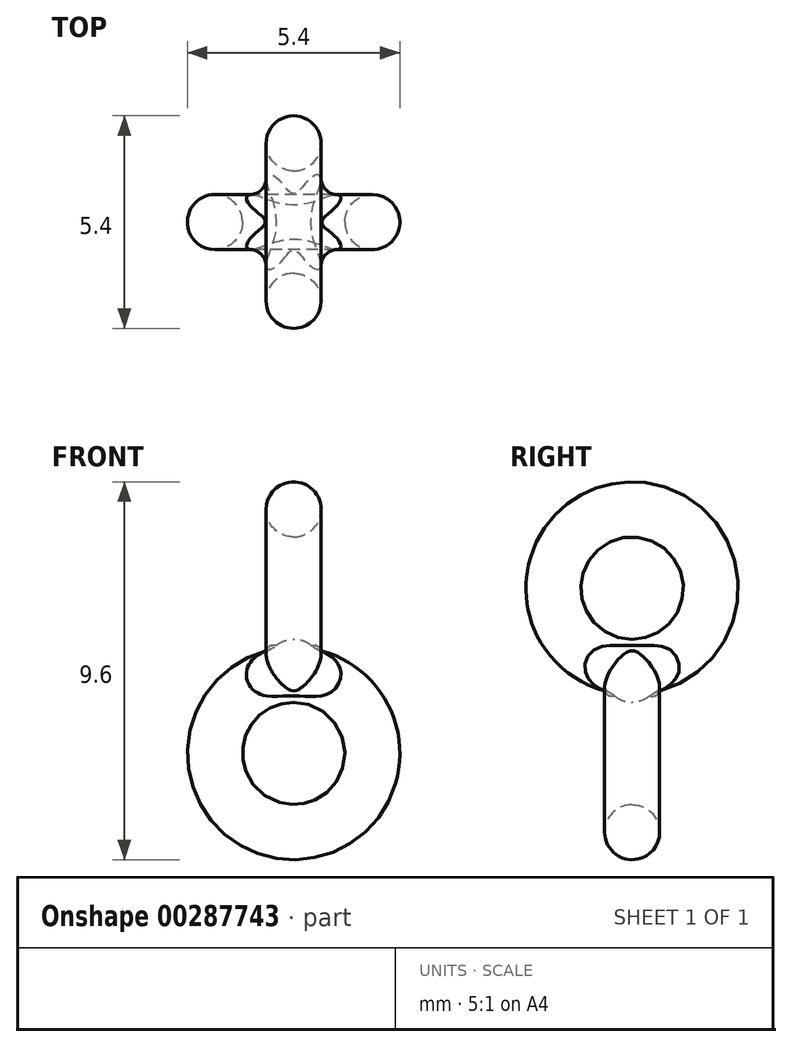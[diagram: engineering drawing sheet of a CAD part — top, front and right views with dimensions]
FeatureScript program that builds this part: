
annotation { "Feature Type Name" : "Feature", "Feature Type Description" : "" }
export const myFeature = defineFeature(function(context is Context, id is Id, definition is map)
    precondition{}
    {
        {
            var Q0;
            Q0=qCreatedBy(makeId("Front.planeOp"),FACE);
            var sketch = newSketch(context, id + "F0", { "sketchPlane" : qUnion([Q0])});
            skCircle(sketch, "E0", {"center": v(0, 0) * mm, "radius": 0.7 * mm});
            skLineSegment(sketch, "E1", {"start": v(0, 2) * mm, "end": v(1.35, 2) * mm, "construction": true});
            skSolve(sketch);
        }
        {
            var Q0;
            Q0 = qSketchRegion(id + "F0", true);
            var Q1;
            Q1=sQuery(id+"F0.wireOp",EDGE,"E1");
            revolve(context, id + "F1", {"entities" : qUnion([Q0]), "axis" : qUnion([Q1]), "revolveType" : RevolveType.FULL});
        }
        {
            var Q0;
            Q0=qCreatedBy(makeId("Right.planeOp"),FACE);
            var sketch = newSketch(context, id + "F2", { "sketchPlane" : qUnion([Q0])});
            skCircle(sketch, "E2", {"center": v(0, -0.2) * mm, "radius": 0.7 * mm});
            skLineSegment(sketch, "E3", {"start": v(0, -2.2) * mm, "end": v(1.4, -2.2) * mm, "construction": true});
            skSolve(sketch);
        }
        {
            var Q0;
            Q0 = qSketchRegion(id + "F2", true);
            var Q1;
            Q1=sQuery(id+"F2.wireOp",EDGE,"E3");
            revolve(context, id + "F3", {"operationType" : NewBodyOperationType.ADD, "entities" : qUnion([Q0]), "axis" : qUnion([Q1]), "revolveType" : RevolveType.FULL});
        }
        {
            var Q0;
            Q0=makeQuery(id+"F3.boolean.opBoolean","INTERSECT",EDGE,{"derivedFrom":[makeQuery(id+"F1.opRevolve","SWEPT_FACE",FACE,{"disambiguationData":[OSD([sQuery(id+"F0.wireOp",EDGE,"E0")])]}),makeQuery(id+"F3.opRevolve","SWEPT_FACE",FACE,{"disambiguationData":[OSD([sQuery(id+"F2.wireOp",EDGE,"E2")])]})]});
            fillet(context, id + "F4", {"entities" : qUnion([Q0]), "radius" : 0.7 * mm, "tangentPropagation" : true, "allowEdgeOverflow" : false});
        }
        {
            var Q0;
            Q0=sQuery(id+"F2.wireOp",VERTEX,"E3.start");
            var Q1;
            Q1=qCreatedBy(makeId("Top.planeOp"),FACE);
            cPlane(context, id + "F5", {"entities" : qUnion([Q0, Q1]), "cplaneType" : CPlaneType.PLANE_POINT, "offset" : 25 * mm, "width" : 150 * mm, "height" : 150 * mm});
        }
        {
            var Q0;
            Q0=qCreatedBy(id+"F5.planeOp",FACE);
            var sketch = newSketch(context, id + "F6", { "sketchPlane" : qUnion([Q0])});
            skLineSegment(sketch, "E4", {"start": v(1.6, -0.7) * mm, "end": v(-1.6, -0.7) * mm});
            skLineSegment(sketch, "E5", {"start": v(1.6, 0.7) * mm, "end": v(-1.6, 0.7) * mm});
            skArc(sketch, "E6", {"start": v(1.56, 0.55) * mm, "mid": v(1.3, 0) * mm, "end": v(1.56, -0.55) * mm});
            skArc(sketch, "E7", {"start": v(-1.56, -0.55) * mm, "mid": v(-1.3, 0) * mm, "end": v(-1.56, 0.55) * mm});
            skSolve(sketch);
        }
    });
